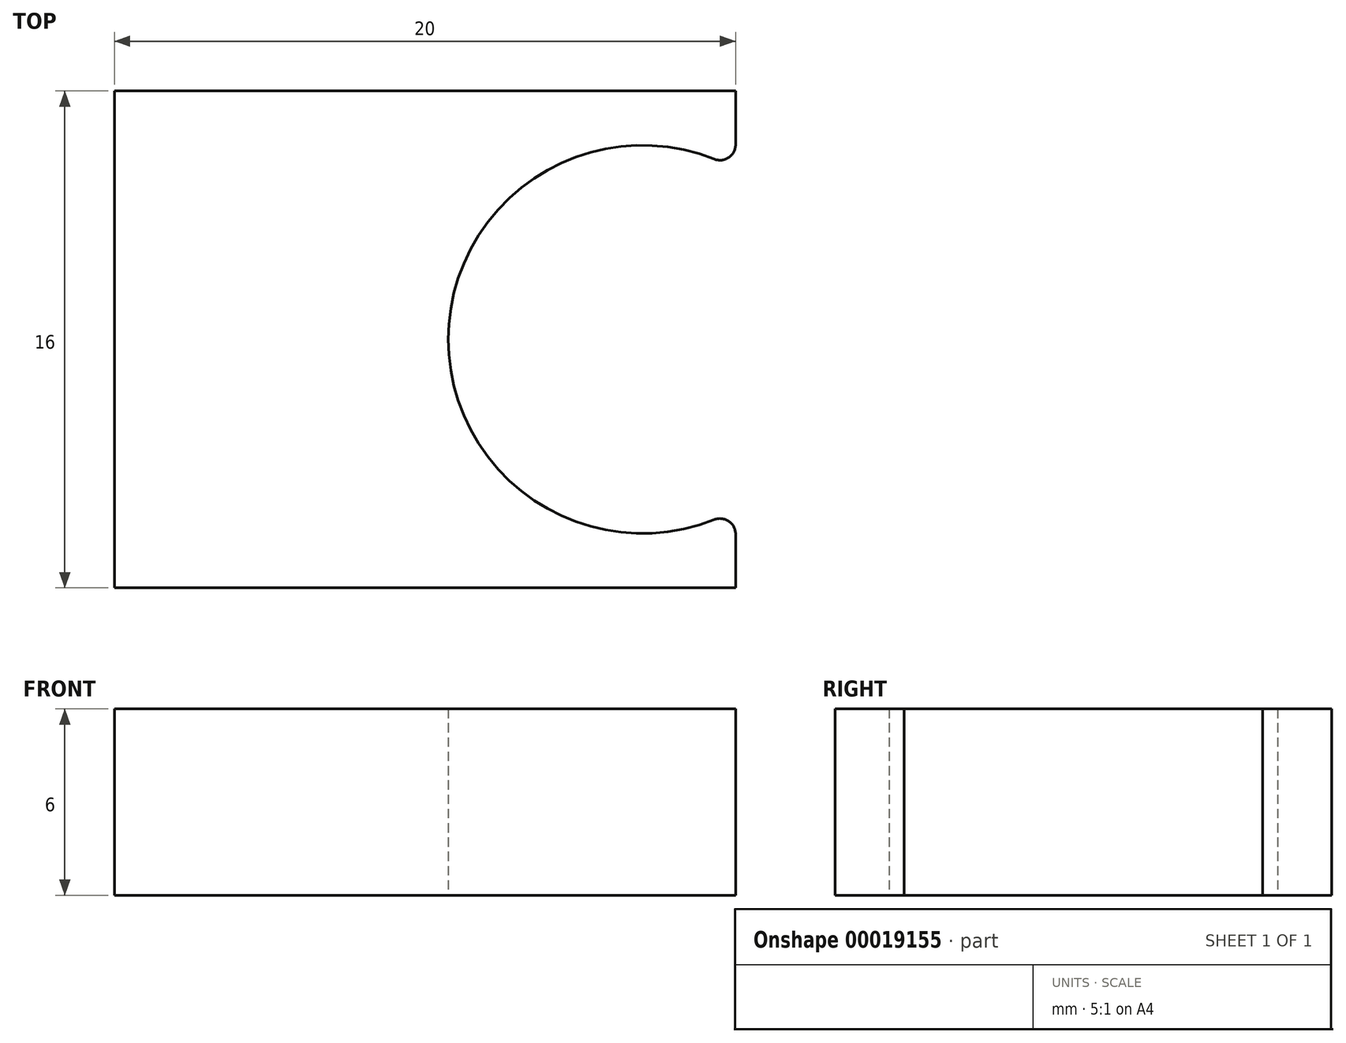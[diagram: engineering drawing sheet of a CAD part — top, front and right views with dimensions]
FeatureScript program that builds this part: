
annotation { "Feature Type Name" : "Feature", "Feature Type Description" : "" }
export const myFeature = defineFeature(function(context is Context, id is Id, definition is map)
    precondition{}
    {
        {
            var Q0;
            Q0=qCreatedBy(makeId("Top.planeOp"),FACE);
            var sketch = newSketch(context, id + "F0", { "sketchPlane" : qUnion([Q0])});
            skArc(sketch, "E0", {"start": v(3, 5.48) * mm, "mid": v(-6.25, 0) * mm, "end": v(3, -5.48) * mm});
            skLineSegment(sketch, "E1.bottom", {"start": v(3, -8) * mm, "end": v(-17, -8) * mm});
            skLineSegment(sketch, "E1.top", {"start": v(3, 8) * mm, "end": v(-17, 8) * mm});
            skLineSegment(sketch, "E1.left", {"start": v(3, -8) * mm, "end": v(3, -5.48) * mm});
            skLineSegment(sketch, "E1.right", {"start": v(-17, -8) * mm, "end": v(-17, 8) * mm});
            skPoint(sketch, "E1.middle", {"position": v(-7, 0) * mm});
            skLineSegment(sketch, "E2.trimOffspring", {"start": v(3, 5.48) * mm, "end": v(3, 8) * mm});
            skSolve(sketch);
        }
        {
            var Q0;
            Q0=makeQuery(id+"F0.imprint","IMPRINT",FACE,{"disambiguationData":[TD([[makeQuery(id+"F0.imprint","IMPRINT",EDGE,{"derivedFrom":sQuery(id+"F0.wireOp",EDGE,"E0")}),-1.0]])]});
            extrude(context, id + "F1", {"entities" : qUnion([Q0]), "depth" : 6 * mm});
        }
        {
            var Q0;
            Q0=makeQuery(id+"F1.opExtrude","SWEPT_EDGE",EDGE,{"disambiguationData":[OSD([sQuery(id+"F0.wireOp",EDGE,"E0"),sQuery(id+"F0.wireOp",EDGE,"E2.trimOffspring")])]});
            var Q1;
            Q1=makeQuery(id+"F1.opExtrude","SWEPT_EDGE",EDGE,{"disambiguationData":[OSD([sQuery(id+"F0.wireOp",EDGE,"E0"),sQuery(id+"F0.wireOp",EDGE,"E1.left")])]});
            fillet(context, id + "F2", {"entities" : qUnion([Q0, Q1]), "radius" : .5 * mm, "tangentPropagation" : true, "allowEdgeOverflow" : false});
        }
    });
